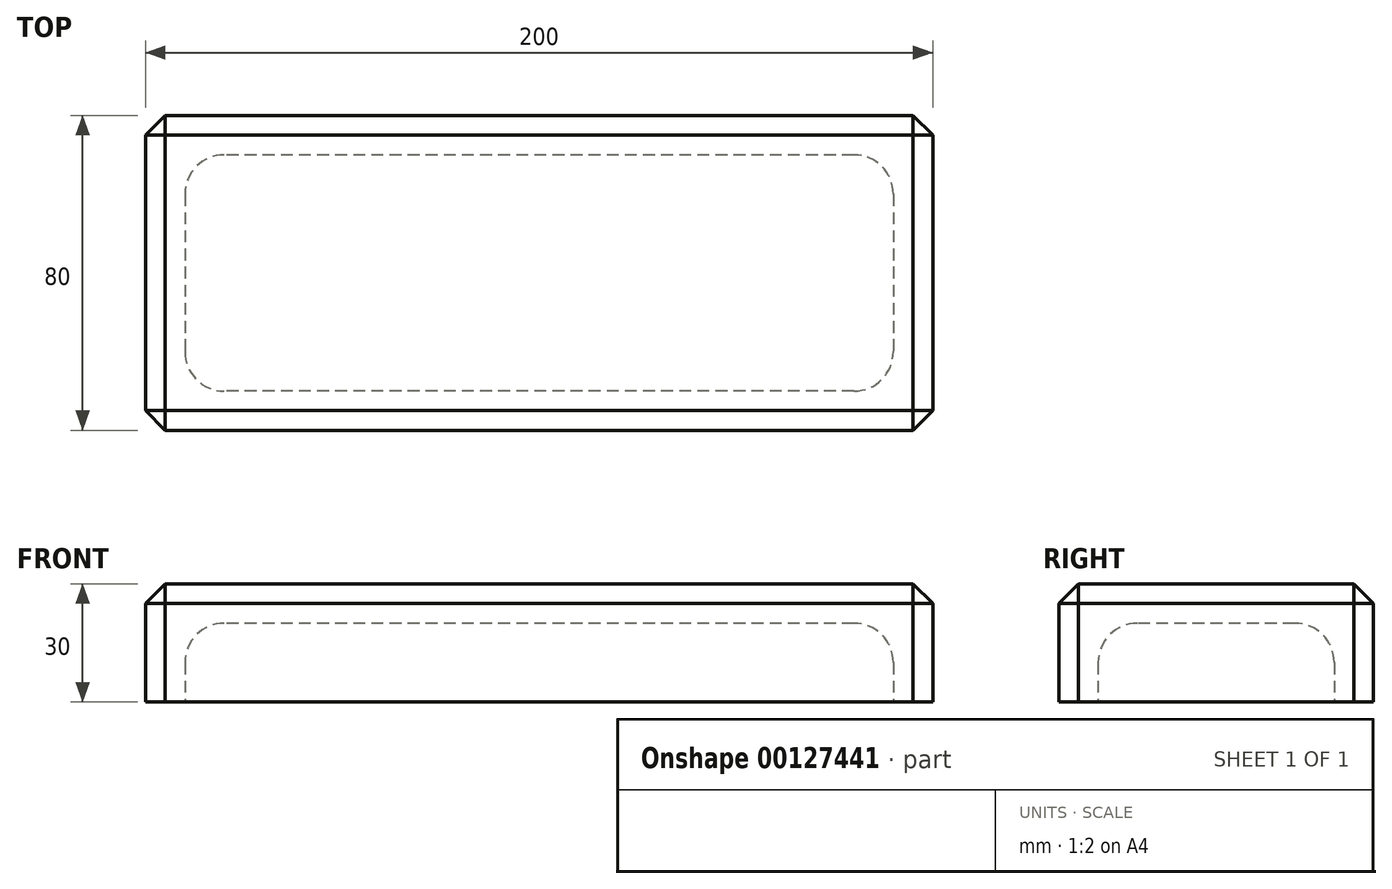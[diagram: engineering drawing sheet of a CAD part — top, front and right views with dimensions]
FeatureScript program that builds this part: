
annotation { "Feature Type Name" : "Feature", "Feature Type Description" : "" }
export const myFeature = defineFeature(function(context is Context, id is Id, definition is map)
    precondition{}
    {
        {
            var Q0;
            Q0=qCreatedBy(makeId("Front.planeOp"),FACE);
            var sketch = newSketch(context, id + "F0", { "sketchPlane" : qUnion([Q0])});
            skLineSegment(sketch, "E0.bottom", {"start": v(100, 15) * mm, "end": v(-100, 15) * mm});
            skLineSegment(sketch, "E0.top", {"start": v(100, -15) * mm, "end": v(-100, -15) * mm});
            skLineSegment(sketch, "E0.left", {"start": v(100, 15) * mm, "end": v(100, -15) * mm});
            skLineSegment(sketch, "E0.right", {"start": v(-100, 15) * mm, "end": v(-100, -15) * mm});
            skPoint(sketch, "E0.middle", {"position": v(0, 0) * mm});
            skSolve(sketch);
        }
        {
            var Q0;
            Q0=qSketchRegion(id+"F0",true);
            extrude(context, id + "F1", {"entities" : qUnion([Q0]), "oppositeDirection" : true, "depth" : 80 * mm});
        }
        {
            var Q0;
            Q0=makeQuery(id+"F1.opExtrude","SWEPT_FACE",FACE,{"disambiguationData":[OSD([sQuery(id+"F0.wireOp",EDGE,"E0.top")])]});
            shell(context, id + "F2", {"entities" : qUnion([Q0]), "thickness" : 10 * mm});
        }
        {
            var Q0;
            {var subQ0=sQuery(id+"F0.wireOp",EDGE,"E0.right");Q0=makeQuery(id+"F2.opShell","OFFSET_EDGE",EDGE,{"disambiguationData":[OSD([subQ0]),TDD([makeQuery(id+"F1.opExtrude","CAP_EDGE",EDGE,{"disambiguationData":[OSD([subQ0])],"isStart":true})])]});}
            var Q1;
            {var subQ0=sQuery(id+"F0.wireOp",EDGE,"E0.bottom");Q1=makeQuery(id+"F2.opShell","OFFSET_EDGE",EDGE,{"disambiguationData":[OSD([subQ0]),TDD([makeQuery(id+"F1.opExtrude","CAP_EDGE",EDGE,{"disambiguationData":[OSD([subQ0])],"isStart":true})])]});}
            var Q2;
            Q2=makeQuery(id+"F2.opShell","OFFSET_EDGE",EDGE,{"disambiguationData":[OSD([sQuery(id+"F0.wireOp",EDGE,"E0.bottom"),sQuery(id+"F0.wireOp",EDGE,"E0.right")])]});
            var Q3;
            {var subQ0=sQuery(id+"F0.wireOp",EDGE,"E0.left");Q3=makeQuery(id+"F2.opShell","OFFSET_EDGE",EDGE,{"disambiguationData":[OSD([subQ0]),TDD([makeQuery(id+"F1.opExtrude","CAP_EDGE",EDGE,{"disambiguationData":[OSD([subQ0])],"isStart":true})])]});}
            var Q4;
            Q4=makeQuery(id+"F2.opShell","OFFSET_EDGE",EDGE,{"disambiguationData":[OSD([sQuery(id+"F0.wireOp",EDGE,"E0.bottom"),sQuery(id+"F0.wireOp",EDGE,"E0.left")])]});
            var Q5;
            {var subQ0=sQuery(id+"F0.wireOp",EDGE,"E0.left");Q5=makeQuery(id+"F2.opShell","OFFSET_EDGE",EDGE,{"disambiguationData":[OSD([subQ0]),TDD([makeQuery(id+"F1.opExtrude","CAP_EDGE",EDGE,{"disambiguationData":[OSD([subQ0])],"isStart":false})])]});}
            var Q6;
            {var subQ0=sQuery(id+"F0.wireOp",EDGE,"E0.bottom");Q6=makeQuery(id+"F2.opShell","OFFSET_EDGE",EDGE,{"disambiguationData":[OSD([subQ0]),TDD([makeQuery(id+"F1.opExtrude","CAP_EDGE",EDGE,{"disambiguationData":[OSD([subQ0])],"isStart":false})])]});}
            var Q7;
            {var subQ0=sQuery(id+"F0.wireOp",EDGE,"E0.right");Q7=makeQuery(id+"F2.opShell","OFFSET_EDGE",EDGE,{"disambiguationData":[OSD([subQ0]),TDD([makeQuery(id+"F1.opExtrude","CAP_EDGE",EDGE,{"disambiguationData":[OSD([subQ0])],"isStart":false})])]});}
            fillet(context, id + "F3", {"entities" : qUnion([Q0, Q1, Q2, Q3, Q4, Q5, Q6, Q7]), "radius" : 10 * mm, "tangentPropagation" : true, "allowEdgeOverflow" : false});
        }
        {
            var Q0;
            Q0=makeQuery(id+"F1.opExtrude","CAP_EDGE",EDGE,{"disambiguationData":[OSD([sQuery(id+"F0.wireOp",EDGE,"E0.right")])],"isStart":true});
            var Q1;
            Q1=makeQuery(id+"F1.opExtrude","CAP_EDGE",EDGE,{"disambiguationData":[OSD([sQuery(id+"F0.wireOp",EDGE,"E0.bottom")])],"isStart":true});
            var Q2;
            Q2=makeQuery(id+"F1.opExtrude","SWEPT_EDGE",EDGE,{"disambiguationData":[OSD([sQuery(id+"F0.wireOp",EDGE,"E0.bottom"),sQuery(id+"F0.wireOp",EDGE,"E0.right")])]});
            var Q3;
            Q3=makeQuery(id+"F1.opExtrude","CAP_EDGE",EDGE,{"disambiguationData":[OSD([sQuery(id+"F0.wireOp",EDGE,"E0.right")])],"isStart":false});
            var Q4;
            Q4=makeQuery(id+"F1.opExtrude","CAP_EDGE",EDGE,{"disambiguationData":[OSD([sQuery(id+"F0.wireOp",EDGE,"E0.bottom")])],"isStart":false});
            var Q5;
            Q5=makeQuery(id+"F1.opExtrude","CAP_EDGE",EDGE,{"disambiguationData":[OSD([sQuery(id+"F0.wireOp",EDGE,"E0.left")])],"isStart":false});
            var Q6;
            Q6=makeQuery(id+"F1.opExtrude","SWEPT_EDGE",EDGE,{"disambiguationData":[OSD([sQuery(id+"F0.wireOp",EDGE,"E0.bottom"),sQuery(id+"F0.wireOp",EDGE,"E0.left")])]});
            var Q7;
            Q7=makeQuery(id+"F1.opExtrude","CAP_EDGE",EDGE,{"disambiguationData":[OSD([sQuery(id+"F0.wireOp",EDGE,"E0.left")])],"isStart":true});
            chamfer(context, id + "F4", {"entities" : qUnion([Q0, Q1, Q2, Q3, Q4, Q5, Q6, Q7]), "width" : 5 * mm, "tangentPropagation" : true});
        }
    });
